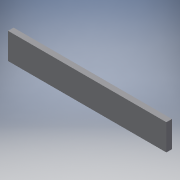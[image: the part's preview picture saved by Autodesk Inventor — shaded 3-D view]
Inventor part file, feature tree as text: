
AUTODESK INVENTOR PART (.ipt)
format: ipt  version: 2018.2 (Build 222227000, 227)  size: 96,256 bytes
history: native  units: in
note: dims shown in document units (in); Inventor stores cm internally (conversion verified against a paired STEP export)
features: other x4, reference x2, extrude x1, sketch x1
ambient origin geometry x8: Origin, YZ Plane, XZ Plane, XY Plane, X Axis, Y Axis, Z Axis, Center Point
bodies: Solid1 (feature_tree)
feature tree (8):
  extrude  "Extrusion1"  Depth=5.0in
  sketch  "Sketch1"  dims[d0=1.0in d1=0.0in d2=28.226in d4=5.0in]
  reference  "Reference1"
  reference  "Reference2"
  parser-record x1  (decoder bookkeeping rows leaked as tree rows — omitted from the tree; the rows remain in map.json)
  other  "Mounting Part figureing outness.iam"
  other  "Plywood Base - Bottom:1"
  other  "2835T310_MIGHTY-LITE CASTER:6"
note: 1 file-system path scrubbed to <path> (originals preserved in map.json)
